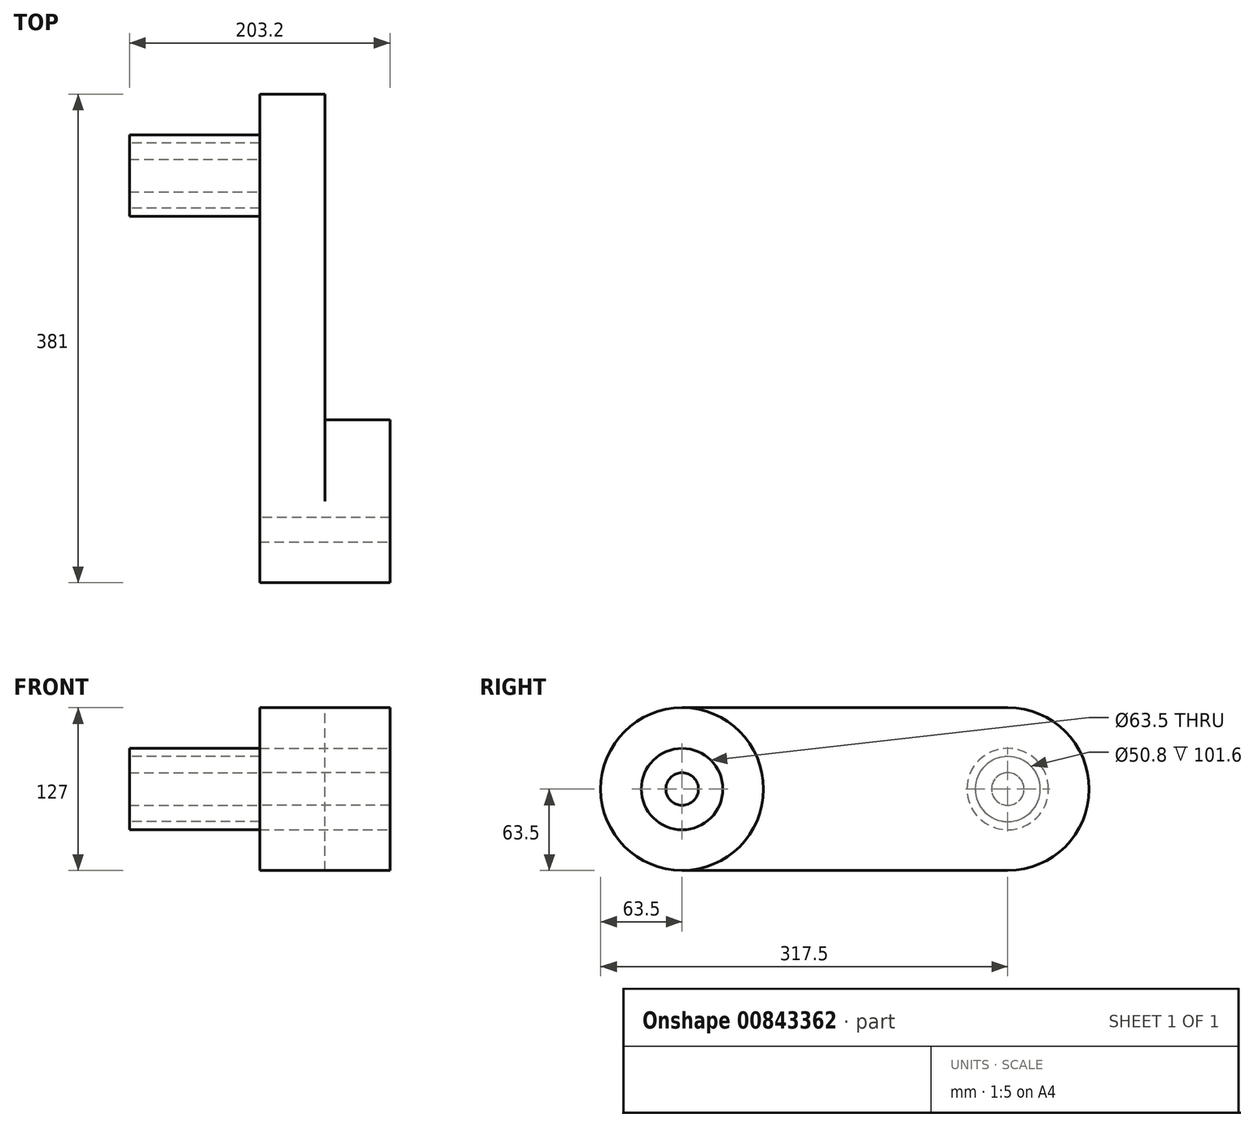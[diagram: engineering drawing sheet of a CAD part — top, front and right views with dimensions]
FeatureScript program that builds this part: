
annotation { "Feature Type Name" : "Feature", "Feature Type Description" : "" }
export const myFeature = defineFeature(function(context is Context, id is Id, definition is map)
    precondition{}
    {
        {
            var Q0;
            Q0=qCreatedBy(makeId("Right.planeOp"),FACE);
            var sketch = newSketch(context, id + "F0", { "sketchPlane" : qUnion([Q0])});
            skLineSegment(sketch, "E0.bottom", {"start": v(0, 0) * mm, "end": v(254, 0) * mm});
            skLineSegment(sketch, "E0.top", {"start": v(0, 127) * mm, "end": v(254, 127) * mm});
            skArc(sketch, "E1", {"start": v(0, 127) * mm, "mid": v(-63.5, 63.5) * mm, "end": v(0, 0) * mm});
            skArc(sketch, "E2", {"start": v(254, 0) * mm, "mid": v(317.5, 63.5) * mm, "end": v(254, 127) * mm});
            skSolve(sketch);
        }
        {
            var Q0;
            Q0=makeQuery(id+"F0.imprint","IMPRINT",FACE,{"disambiguationData":[TD([[makeQuery(id+"F0.imprint","IMPRINT",EDGE,{"derivedFrom":sQuery(id+"F0.wireOp",EDGE,"E0.bottom")}),1.0]])]});
            extrude(context, id + "F1", {"entities" : qUnion([Q0]), "depth" : 50.8 * mm, "offsetDistance" : 25.4 * mm});
        }
        {
            var Q0;
            Q0=makeQuery(id+"F1.opExtrude","CAP_FACE",FACE,{"disambiguationData":[OSD([sQuery(id+"F0.wireOp",EDGE,"E0.bottom"),sQuery(id+"F0.wireOp",EDGE,"E0.top"),sQuery(id+"F0.wireOp",EDGE,"E1"),sQuery(id+"F0.wireOp",EDGE,"E2")])],"isStart":false});
            var sketch = newSketch(context, id + "F2", { "sketchPlane" : qUnion([Q0])});
            skCircle(sketch, "E3", {"center": v(0, 63.5) * mm, "radius": 63.5 * mm});
            skSolve(sketch);
        }
        {
            var Q0;
            {var subQ0=sQuery(id+"F2.wireOp",EDGE,"E3");var subQ1=makeQuery(id+"F2.imprint","INTERSECT",VERTEX,{"derivedFrom":[makeQuery(id+"F1.opExtrude","CAP_EDGE",EDGE,{"disambiguationData":[OSD([sQuery(id+"F0.wireOp",EDGE,"E0.bottom")])],"isStart":false}),subQ0]});Q0=makeQuery(id+"F2.imprint","IMPRINT",FACE,{"disambiguationData":[TD([[makeQuery(id+"F2.imprint","IMPRINT",EDGE,{"disambiguationData":[TD([[subQ1,1.0]])],"derivedFrom":subQ0}),1.0]])]});}
            extrude(context, id + "F3", {"entities" : qUnion([Q0]), "operationType" : NewBodyOperationType.ADD, "depth" : 50.8 * mm, "offsetDistance" : 25.4 * mm});
        }
        {
            var Q0;
            Q0=makeQuery(id+"F3.opExtrude","CAP_FACE",FACE,{"disambiguationData":[OSD([sQuery(id+"F2.wireOp",EDGE,"E3")])],"isStart":false});
            var sketch = newSketch(context, id + "F4", { "sketchPlane" : qUnion([Q0])});
            skCircle(sketch, "E4", {"center": v(0, 63.5) * mm, "radius": 31.75 * mm});
            skSolve(sketch);
        }
        {
            var Q0;
            Q0=makeQuery(id+"F4.imprint","IMPRINT",FACE,{"disambiguationData":[TD([[makeQuery(id+"F4.imprint","IMPRINT",EDGE,{"derivedFrom":sQuery(id+"F4.wireOp",EDGE,"E4")}),1.0]])]});
            extrude(context, id + "F5", {"entities" : qUnion([Q0]), "operationType" : NewBodyOperationType.REMOVE, "endBound" : BoundingType.THROUGH_ALL, "oppositeDirection" : true, "depth" : 25.4 * mm, "offsetDistance" : 25.4 * mm});
        }
        {
            var Q0;
            Q0=makeQuery(id+"F1.opExtrude","CAP_FACE",FACE,{"disambiguationData":[OSD([sQuery(id+"F0.wireOp",EDGE,"E0.bottom"),sQuery(id+"F0.wireOp",EDGE,"E0.top"),sQuery(id+"F0.wireOp",EDGE,"E1"),sQuery(id+"F0.wireOp",EDGE,"E2")])],"isStart":true});
            var sketch = newSketch(context, id + "F6", { "sketchPlane" : qUnion([Q0])});
            skCircle(sketch, "E5", {"center": v(-254, 63.5) * mm, "radius": 31.75 * mm});
            skSolve(sketch);
        }
        {
            var Q0;
            Q0=makeQuery(id+"F6.imprint","IMPRINT",FACE,{"disambiguationData":[TD([[makeQuery(id+"F6.imprint","IMPRINT",EDGE,{"derivedFrom":sQuery(id+"F6.wireOp",EDGE,"E5")}),1.0]])]});
            extrude(context, id + "F7", {"entities" : qUnion([Q0]), "operationType" : NewBodyOperationType.ADD, "depth" : 101.6 * mm, "offsetDistance" : 25.4 * mm});
        }
        {
            var Q0;
            Q0=makeQuery(id+"F7.opExtrude","CAP_FACE",FACE,{"disambiguationData":[OSD([sQuery(id+"F6.wireOp",EDGE,"E5")])],"isStart":false});
            var sketch = newSketch(context, id + "F8", { "sketchPlane" : qUnion([Q0])});
            skCircle(sketch, "E6", {"center": v(-254, 63.5) * mm, "radius": 25.4 * mm});
            skSolve(sketch);
        }
        {
            var Q0;
            Q0 = qSketchRegion(id + "F8", true);
            var Q1;
            Q1=makeQuery(id+"F1.opExtrude","CAP_FACE",FACE,{"disambiguationData":[OSD([sQuery(id+"F0.wireOp",EDGE,"E0.bottom"),sQuery(id+"F0.wireOp",EDGE,"E0.top"),sQuery(id+"F0.wireOp",EDGE,"E1"),sQuery(id+"F0.wireOp",EDGE,"E2")])],"isStart":true});
            extrude(context, id + "F9", {"entities" : qUnion([Q0]), "operationType" : NewBodyOperationType.REMOVE, "endBound" : BoundingType.UP_TO_SURFACE, "oppositeDirection" : true, "depth" : 25.4 * mm, "endBoundEntityFace" : qUnion([Q1]), "offsetDistance" : 25.4 * mm});
        }
        {
            var Q0;
            Q0=makeQuery(id+"F1.opExtrude","CAP_FACE",FACE,{"disambiguationData":[OSD([sQuery(id+"F0.wireOp",EDGE,"E0.bottom"),sQuery(id+"F0.wireOp",EDGE,"E0.top"),sQuery(id+"F0.wireOp",EDGE,"E1"),sQuery(id+"F0.wireOp",EDGE,"E2")])],"isStart":true});
            var sketch = newSketch(context, id + "F10", { "sketchPlane" : qUnion([Q0])});
            skCircle(sketch, "E7", {"center": v(-254, 63.5) * mm, "radius": 12.7 * mm});
            skSolve(sketch);
        }
        {
            var Q0;
            Q0=makeQuery(id+"F10.imprint","IMPRINT",FACE,{"disambiguationData":[TD([[makeQuery(id+"F10.imprint","IMPRINT",EDGE,{"derivedFrom":sQuery(id+"F10.wireOp",EDGE,"E7")}),1.0]])]});
            extrude(context, id + "F11", {"entities" : qUnion([Q0]), "operationType" : NewBodyOperationType.ADD, "depth" : 101.6 * mm, "offsetDistance" : 25.4 * mm});
        }
        {
            var Q0;
            Q0=makeQuery(id+"F1.opExtrude","CAP_FACE",FACE,{"disambiguationData":[OSD([sQuery(id+"F0.wireOp",EDGE,"E0.bottom"),sQuery(id+"F0.wireOp",EDGE,"E0.top"),sQuery(id+"F0.wireOp",EDGE,"E1"),sQuery(id+"F0.wireOp",EDGE,"E2")])],"isStart":true});
            var sketch = newSketch(context, id + "F12", { "sketchPlane" : qUnion([Q0])});
            skCircle(sketch, "E8", {"center": v(0, 63.5) * mm, "radius": 12.7 * mm});
            skSolve(sketch);
        }
        {
            var Q0;
            Q0 = qSketchRegion(id + "F12", true);
            extrude(context, id + "F13", {"entities" : qUnion([Q0]), "oppositeDirection" : true, "depth" : 101.6 * mm, "offsetDistance" : 25.4 * mm});
        }
    });
